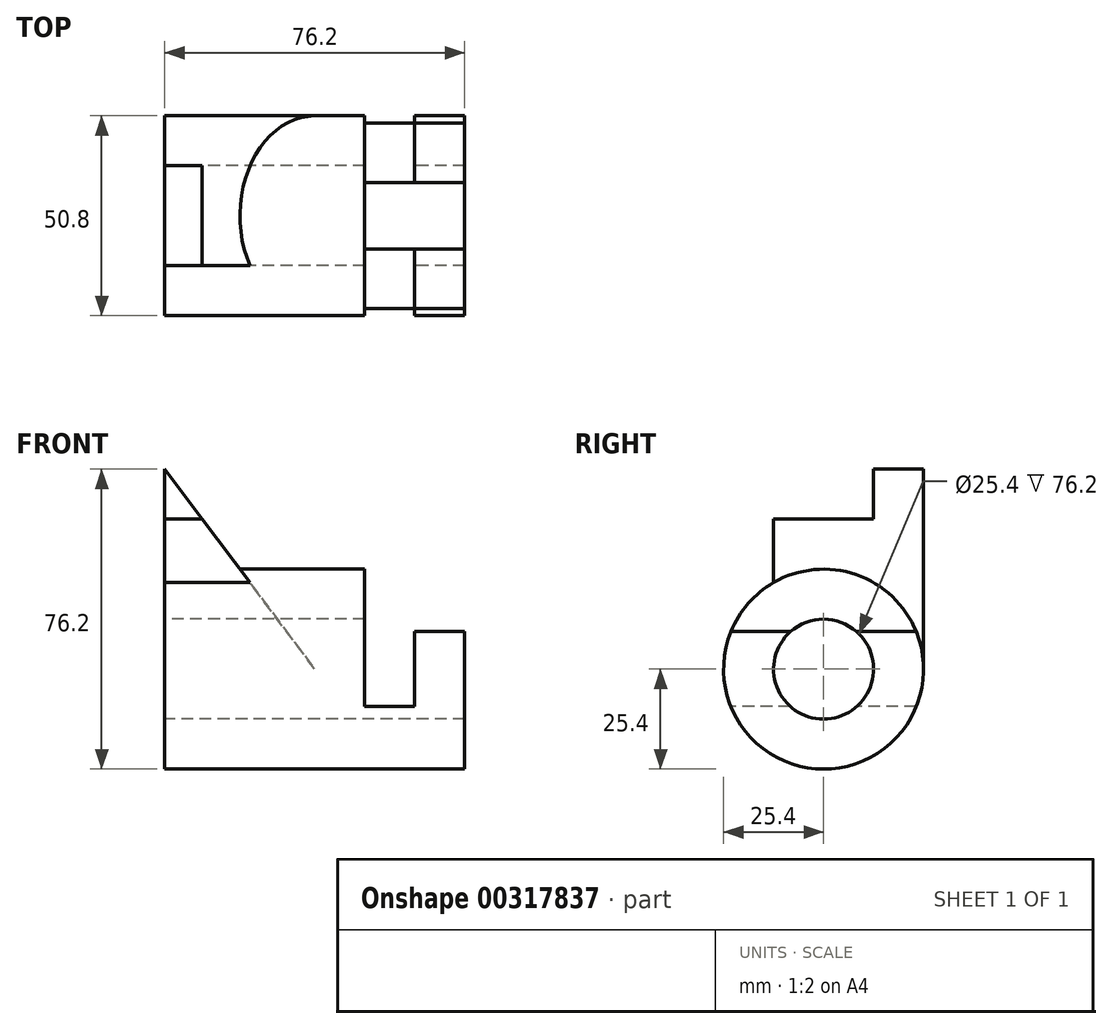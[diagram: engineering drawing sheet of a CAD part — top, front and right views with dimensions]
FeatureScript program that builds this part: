
annotation { "Feature Type Name" : "Feature", "Feature Type Description" : "" }
export const myFeature = defineFeature(function(context is Context, id is Id, definition is map)
    precondition{}
    {
        {
            var Q0;
            Q0=qCreatedBy(makeId("Right.planeOp"),FACE);
            var sketch = newSketch(context, id + "F0", { "sketchPlane" : qUnion([Q0])});
            skCircle(sketch, "E0", {"center": v(0, 0) * mm, "radius": 25.4 * mm});
            skCircle(sketch, "E1", {"center": v(0, 0) * mm, "radius": 12.7 * mm});
            skSolve(sketch);
        }
        {
            var Q0;
            Q0 = qSketchRegion(id + "F0", true);
            extrude(context, id + "F1", {"entities" : qUnion([Q0]), "endBound" : BoundingType.SYMMETRIC, "depth" : 76.2 * mm});
        }
        {
            var Q0;
            Q0=qCreatedBy(makeId("Front.planeOp"),FACE);
            var sketch = newSketch(context, id + "F2", { "sketchPlane" : qUnion([Q0])});
            skLineSegment(sketch, "E2", {"start": v(-38.1, 50.8) * mm, "end": v(-38.1, 0) * mm});
            skLineSegment(sketch, "E3", {"start": v(-38.1, 0) * mm, "end": v(0, 0) * mm});
            skLineSegment(sketch, "E4", {"start": v(0, 0) * mm, "end": v(-38.1, 50.8) * mm});
            skSolve(sketch);
        }
        {
            var Q0;
            Q0 = qSketchRegion(id + "F2", true);
            extrude(context, id + "F3", {"entities" : qUnion([Q0]), "operationType" : NewBodyOperationType.ADD, "depth" : 12.7 * mm, "hasSecondDirection" : true, "secondDirectionOppositeDirection" : true, "secondDirectionDepth" : 25.4 * mm});
        }
        {
            var Q0;
            Q0=qCreatedBy(makeId("Right.planeOp"),FACE);
            var sketch = newSketch(context, id + "F4", { "sketchPlane" : qUnion([Q0])});
            skCircle(sketch, "E5", {"center": v(0, 0) * mm, "radius": 12.7 * mm});
            skSolve(sketch);
        }
        {
            var Q0;
            Q0 = qSketchRegion(id + "F4", true);
            extrude(context, id + "F5", {"entities" : qUnion([Q0]), "operationType" : NewBodyOperationType.REMOVE, "endBound" : BoundingType.THROUGH_ALL, "oppositeDirection" : true, "depth" : 25.4 * mm});
        }
        {
            var Q0;
            Q0=qCreatedBy(makeId("Right.planeOp"),FACE);
            var sketch = newSketch(context, id + "F6", { "sketchPlane" : qUnion([Q0])});
            skLineSegment(sketch, "E6.0", {"start": v(-12.7, 50.8) * mm, "end": v(25.4, 50.8) * mm});
            skLineSegment(sketch, "E7.bottom", {"start": v(-12.7, 50.8) * mm, "end": v(12.7, 50.8) * mm});
            skLineSegment(sketch, "E7.top", {"start": v(-12.7, 38.1) * mm, "end": v(12.7, 38.1) * mm});
            skLineSegment(sketch, "E7.left", {"start": v(-12.7, 50.8) * mm, "end": v(-12.7, 38.1) * mm});
            skLineSegment(sketch, "E7.right", {"start": v(12.7, 50.8) * mm, "end": v(12.7, 38.1) * mm});
            skSolve(sketch);
        }
        {
            var Q0;
            Q0 = qSketchRegion(id + "F6", true);
            extrude(context, id + "F7", {"entities" : qUnion([Q0]), "operationType" : NewBodyOperationType.REMOVE, "endBound" : BoundingType.THROUGH_ALL, "oppositeDirection" : true, "depth" : 25.4 * mm});
        }
        {
            var Q0;
            Q0=qCreatedBy(makeId("Front.planeOp"),FACE);
            var sketch = newSketch(context, id + "F8", { "sketchPlane" : qUnion([Q0])});
            skLineSegment(sketch, "E8", {"start": v(12.7, 25.4) * mm, "end": v(38.1, 25.4) * mm});
            skLineSegment(sketch, "E9", {"start": v(12.7, 25.4) * mm, "end": v(12.7, -9.53) * mm});
            skLineSegment(sketch, "E10", {"start": v(12.7, -9.53) * mm, "end": v(25.4, -9.53) * mm});
            skLineSegment(sketch, "E11", {"start": v(25.4, -9.53) * mm, "end": v(25.4, 9.53) * mm});
            skLineSegment(sketch, "E12", {"start": v(25.4, 9.53) * mm, "end": v(38.1, 9.53) * mm});
            skLineSegment(sketch, "E13", {"start": v(38.1, 9.53) * mm, "end": v(38.1, 25.4) * mm});
            skLineSegment(sketch, "E14.0", {"start": v(38.1, 25.4) * mm, "end": v(38.1, 9.53) * mm});
            skPoint(sketch, "E15.orphan", {"position": v(38.1, -25.4) * mm});
            skSolve(sketch);
        }
        {
            var Q0;
            Q0 = qSketchRegion(id + "F8", true);
            extrude(context, id + "F9", {"entities" : qUnion([Q0]), "operationType" : NewBodyOperationType.REMOVE, "endBound" : BoundingType.THROUGH_ALL, "oppositeDirection" : true, "depth" : 25.4 * mm, "hasSecondDirection" : true, "secondDirectionBound" : SecondDirectionBoundingType.THROUGH_ALL, "secondDirectionOppositeDirection" : false, "secondDirectionDepth" : 25.4 * mm});
        }
    });
